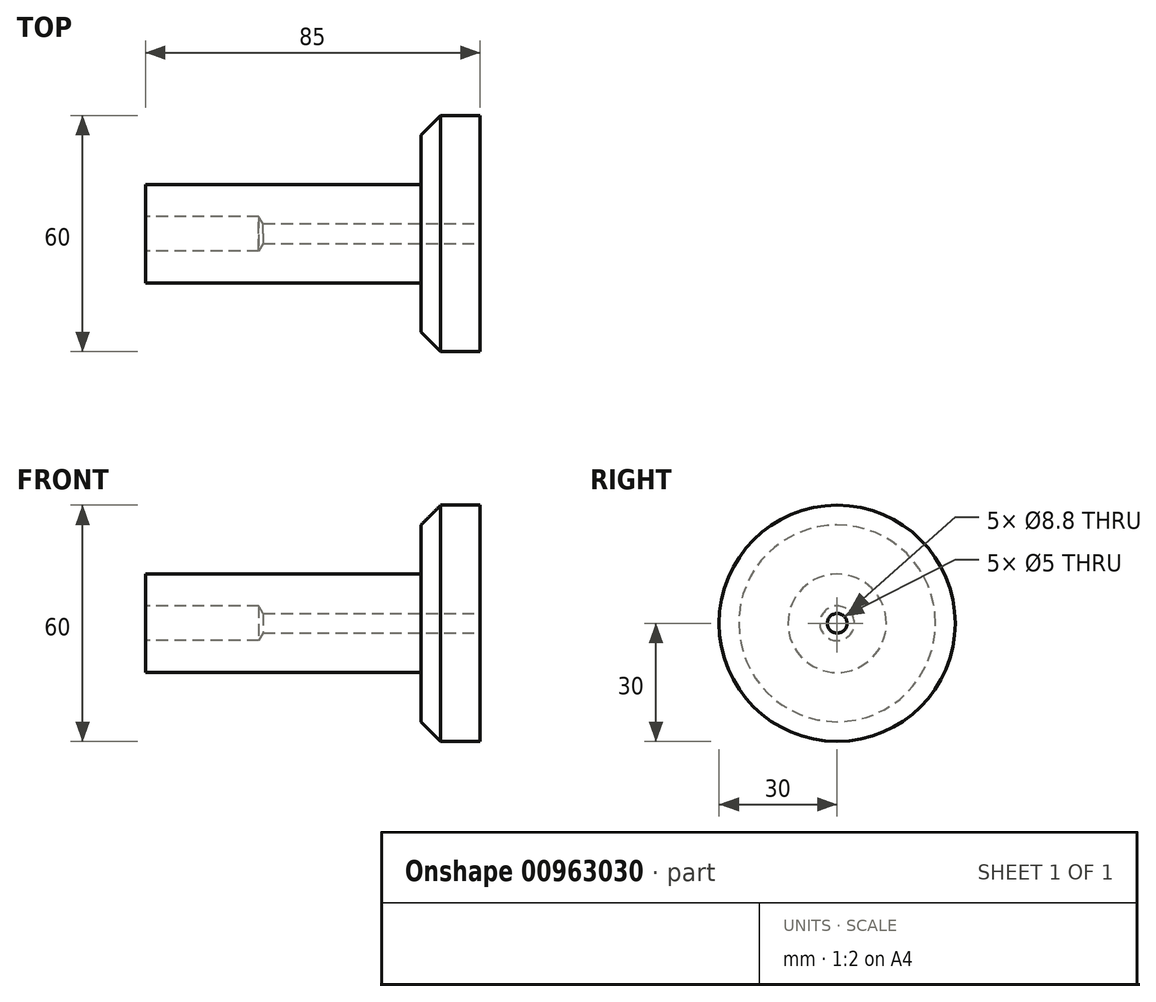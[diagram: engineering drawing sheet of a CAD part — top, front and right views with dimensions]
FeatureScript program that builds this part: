
annotation { "Feature Type Name" : "Feature", "Feature Type Description" : "" }
export const myFeature = defineFeature(function(context is Context, id is Id, definition is map)
    precondition{}
    {
        {
            var Q0;
            Q0=qCreatedBy(makeId("Front.planeOp"),FACE);
            var sketch = newSketch(context, id + "F0", { "sketchPlane" : qUnion([Q0])});
            skLineSegment(sketch, "E0", {"start": v(-46.2, 12.5) * mm, "end": v(23.8, 12.5) * mm});
            skLineSegment(sketch, "E1", {"start": v(23.8, 12.5) * mm, "end": v(23.8, 25) * mm});
            skLineSegment(sketch, "E2", {"start": v(23.8, 25) * mm, "end": v(28.8, 30) * mm});
            skLineSegment(sketch, "E3", {"start": v(28.8, 30) * mm, "end": v(38.8, 30) * mm});
            skPoint(sketch, "E4.orphan", {"position": v(38.8, 0) * mm});
            skLineSegment(sketch, "E5", {"start": v(-68.28, 0) * mm, "end": v(66.52, 0) * mm});
            skLineSegment(sketch, "E6", {"start": v(-46.2, 12.5) * mm, "end": v(-46.2, 0) * mm});
            skLineSegment(sketch, "E7", {"start": v(38.8, 30) * mm, "end": v(38.8, 0) * mm});
            skSolve(sketch);
        }
        {
            var Q0;
            Q0=makeQuery(id+"F0.imprint","IMPRINT",FACE,{"disambiguationData":[TD([[makeQuery(id+"F0.imprint","IMPRINT",EDGE,{"derivedFrom":sQuery(id+"F0.wireOp",EDGE,"i0xrVvDF-YWy9-J3nw-HAGZ-88DrFOi1Weiw")}),-1.0]])]});
            var Q1;
            Q1=makeQuery(id+"F0.imprint","IMPRINT",FACE,{"disambiguationData":[TD([[makeQuery(id+"F0.imprint","IMPRINT",EDGE,{"derivedFrom":sQuery(id+"F0.wireOp",EDGE,"E0")}),-1.0]])]});
            var Q2;
            Q2=sQuery(id+"F0.wireOp",EDGE,"E5");
            revolve(context, id + "F1", {"surfaceOperationType" : NewSurfaceOperationType.NEW, "entities" : qUnion([Q0, Q1]), "axis" : qUnion([Q2]), "revolveType" : RevolveType.FULL});
        }
        {
            var Q0;
            Q0=makeQuery(id+"F1.opRevolve","SWEPT_FACE",FACE,{"disambiguationData":[OSD([sQuery(id+"F0.wireOp",EDGE,"E6")])]});
            var sketch = newSketch(context, id + "F2", { "sketchPlane" : qUnion([Q0])});
            skCircle(sketch, "E8", {"center": v(0, 0) * mm, "radius": 4.38 * mm});
            skSolve(sketch);
        }
        {
            var Q0;
            Q0=sQuery(id+"F2.wireOp",VERTEX,"E8.center");
            var Q1;
            Q1=makeQuery(id+"F1.opRevolve","SWEPT_BODY",BODY,{"disambiguationData":[OSD([sQuery(id+"F0.wireOp",EDGE,"E0"),sQuery(id+"F0.wireOp",EDGE,"E1"),sQuery(id+"F0.wireOp",EDGE,"E2"),sQuery(id+"F0.wireOp",EDGE,"E3"),sQuery(id+"F0.wireOp",EDGE,"E5"),sQuery(id+"F0.wireOp",EDGE,"E6"),sQuery(id+"F0.wireOp",EDGE,"E7")])]});
            hole(context, id + "F3", {"style" : HoleStyle.SIMPLE, "endStyle" : HoleEndStyle.BLIND, "standardTappedOrClearance" : lookupTablePath({ "standard" : "ISO", "engagement" : "75%", "pitch" : "1.25 mm", "size" : "M10", "type" : "Tapped" }), "standardBlindInLast" : lookupTablePath({ "standard" : "ISO", "fit" : "Normal", "engagement" : "75%", "pitch" : "1.25 mm", "size" : "M10", "type" : "Clearance & tapped" }), "holeDiameter" : 8.8 * mm, "majorDiameter" : 10 * mm, "showTappedDepth" : true, "holeDepth" : 28.75 * mm, "isTappedThrough" : true, "tappedDepth" : 25 * mm, "tapClearance" : 3, "startFromSketch" : true, "locations" : qUnion([Q0]), "scope" : qUnion([Q1])});
        }
        {
            var Q0;
            Q0=makeQuery(id+"F1.opRevolve","SWEPT_FACE",FACE,{"disambiguationData":[OSD([sQuery(id+"F0.wireOp",EDGE,"E7")])]});
            var sketch = newSketch(context, id + "F4", { "sketchPlane" : qUnion([Q0])});
            skCircle(sketch, "E9", {"center": v(0, 0) * mm, "radius": 2.5 * mm});
            skSolve(sketch);
        }
        {
            var Q0;
            Q0=sQuery(id+"F4.wireOp",VERTEX,"E9.center");
            var Q1;
            Q1=makeQuery(id+"F1.opRevolve","SWEPT_BODY",BODY,{"disambiguationData":[OSD([sQuery(id+"F0.wireOp",EDGE,"E0"),sQuery(id+"F0.wireOp",EDGE,"E1"),sQuery(id+"F0.wireOp",EDGE,"E2"),sQuery(id+"F0.wireOp",EDGE,"E3"),sQuery(id+"F0.wireOp",EDGE,"E5"),sQuery(id+"F0.wireOp",EDGE,"E6"),sQuery(id+"F0.wireOp",EDGE,"E7")])]});
            hole(context, id + "F5", {"style" : HoleStyle.SIMPLE, "endStyle" : HoleEndStyle.THROUGH, "standardTappedOrClearance" : lookupTablePath({ "standard" : "ISO", "size" : "5", "type" : "Drilled" }), "standardBlindInLast" : lookupTablePath({ "standard" : "ISO", "size" : "5", "type" : "Drilled" }), "holeDiameter" : 5 * mm, "majorDiameter" : 5 * mm, "isTappedThrough" : true, "tappedDepth" : 25 * mm, "tapClearance" : 3, "startFromSketch" : true, "locations" : qUnion([Q0]), "scope" : qUnion([Q1])});
        }
    });
